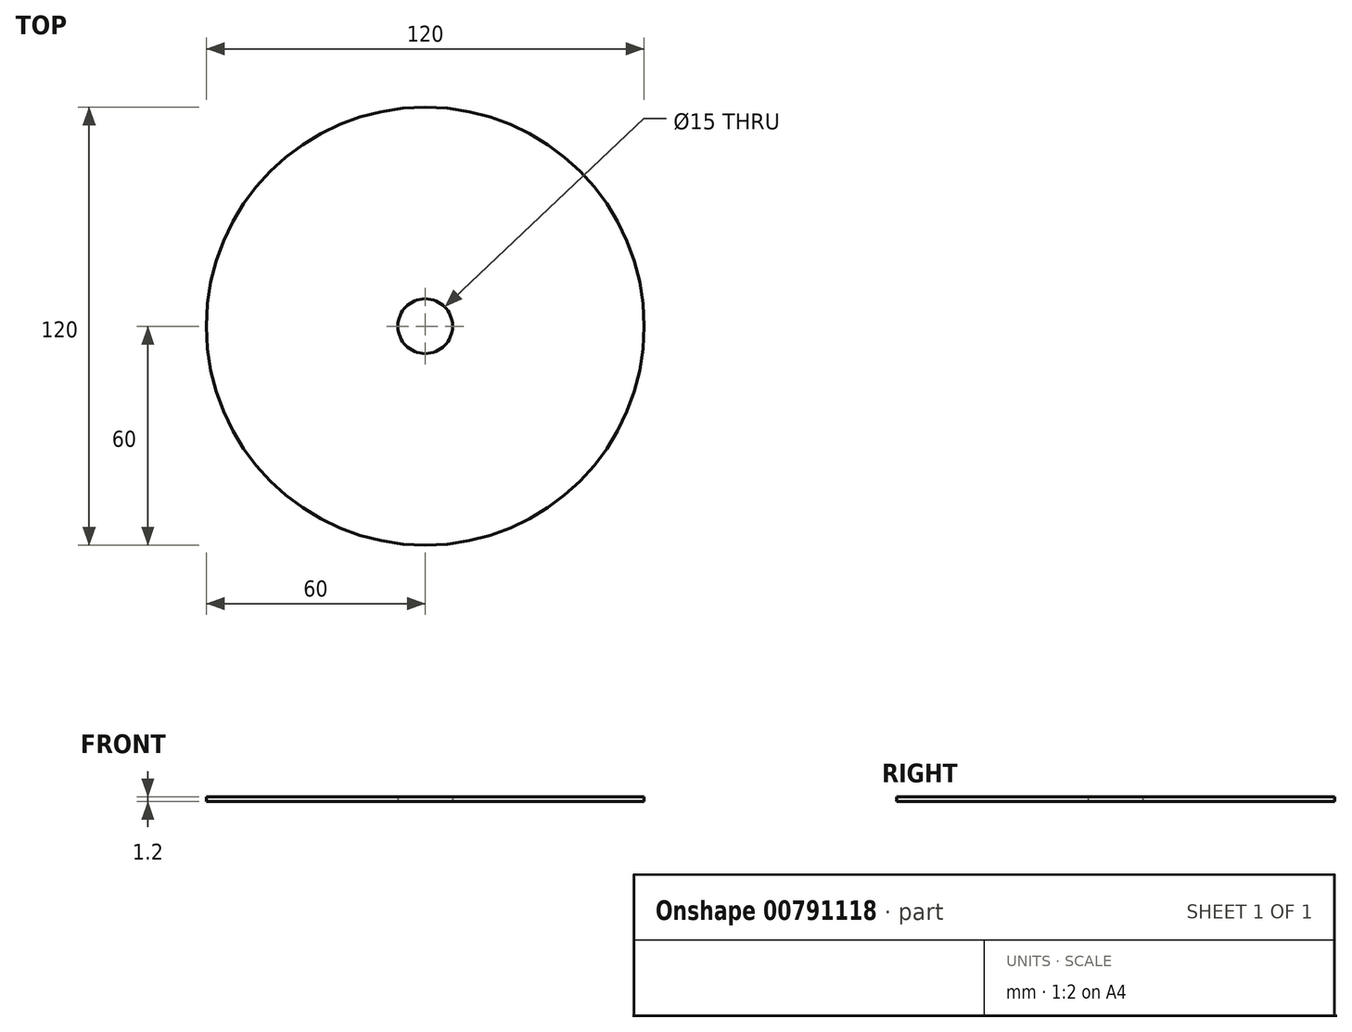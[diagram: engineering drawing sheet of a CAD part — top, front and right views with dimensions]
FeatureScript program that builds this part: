
annotation { "Feature Type Name" : "Feature", "Feature Type Description" : "" }
export const myFeature = defineFeature(function(context is Context, id is Id, definition is map)
    precondition{}
    {
        {
            var Q0;
            Q0=qCreatedBy(makeId("Top.planeOp"),FACE);
            var sketch = newSketch(context, id + "F0", { "sketchPlane" : qUnion([Q0])});
            skCircle(sketch, "E0", {"center": v(0, 0) * mm, "radius": 60 * mm});
            skCircle(sketch, "E1", {"center": v(0, 0) * mm, "radius": 7.5 * mm});
            skSolve(sketch);
        }
        {
            var Q0;
            Q0 = qSketchRegion(id + "F0", true);
            extrude(context, id + "F1", {"entities" : qUnion([Q0]), "depth" : 1.2 * mm, "offsetDistance" : 25 * mm});
        }
    });
